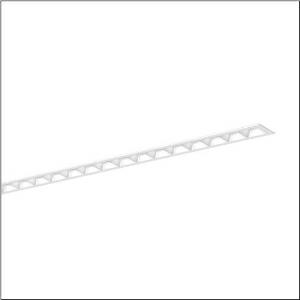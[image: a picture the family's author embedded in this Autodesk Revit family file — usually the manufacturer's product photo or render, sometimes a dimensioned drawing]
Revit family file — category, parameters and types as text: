
# Revit family: silica_21_51mx16db35wb
name_source: partatom
category: Lighting Fixtures
units: mm (PartAtom-declared; Revit-internal decimal feet)

## family parameters
Cut with Voids When Loaded = No
Host = Face
Light Source = No
Part Type = Normal
Room Calculation Point = No
Round Connector Dimension = Use Diameter
Shared = No

## types (1)
- --- (1 x LED, 5400 lm, 31.4 W, 3000K)
    Apparent Load = 31 VA
    CIE Flux Codes = 83 98 100 100 100
    Color Rendering = 80
    Color Temperature = 3000K
    Default Elevation = 1800 mm
    Description = Silica 21, office luminaire, primary light control with darklight reflector, of PMMA, white, CAT 2 (L<= 3000cd/m²), light emission: direct distribution, primary light characteristic: symmetric, installation type: recessed, LED, rated luminous flux: 5.400lm, luminous efficacy: 172lm/W, light colour: 830, colour temperature: 3000K, control gear: DALI 2, with terminal, 3+2-pole, max. 2.5mm², mains connection: 220..240V, AC, 50/60Hz, rated input power: 31.4W, luminaire housing, of aluminium, traffic white (RAL 9016), length: 1.528mm, width: 79mm, height: 53mm, protection rating (complete): IP20, insulation class (complete): insulation class I (protective earthing), certification: CE, ENEC, VDE, permissible operating ambient temperature: 0..+35°C, standard: EN 50419, packaging unit: 1 piece
    Height = 0 mm  [stored 0 ft]
    Lamp = 1 x LED
    Lamp Light Flux = 5400 lm
    Lamp Power = 31.4 W
    Lamp count = 1
    Length = 1527 mm
    Luminous efficacy = 172 lm/W
    Manufacturer = Siteco
    ModVariant = No
    Model = 51MX16DB35WB
    Mounting Place = Ceiling
    Mounting Type = Recessed
    Number of Poles = 1
    OnlyDefault = Yes
    Power Factor = 1
    Product Name = Silica 21
    Product group = office luminaire | ceiling recessed
    ProductGroupID = 400
    Protection Class = Protection class I
    Protection Degree = IP 20
    RLX_Detail_Level = 1
    RLX_Emergency_Light_Flux = 0 lm
    RLX_Emergency_Type = 0
    RLX_Emergency_Type_DB = No
    RlxData = <blob elided: 39445 chars, md5=df7443c5>
    Socket = socket
    Standby Power = 0 W
    System Light Flux = 5400 lm
    System Power = 31 W
    Type Comments = factory setting: luminous flux: 100 % | dim-lin: 254 | 360 mA
    Type Image = l_1335884.jpg
    URL = http://relux.com
    VarID = @adj_124251
    Voltage = 0 V
    Weight = 0.00 kg
    Width = 79 mm

note: [stored X ft] marks values corroborated as IEEE doubles in the binary element streams (Revit-internal decimal feet)

## geometry (parser evidence)
native form markers: Blend x4, Sweep x9
no freeform markers — native parametric forms only
